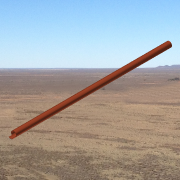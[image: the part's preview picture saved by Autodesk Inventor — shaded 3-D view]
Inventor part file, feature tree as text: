
AUTODESK INVENTOR PART (.ipt)
format: ipt  version: 2013 SP2 (Build 170200200, 200)  size: 152,576 bytes
history: native  units: in
note: dims shown in document units (in); Inventor stores cm internally (conversion verified against a paired STEP export)
features: sketch x4, extrude x3, plane x1
ambient origin geometry x8: Origin, YZ Plane, XZ Plane, XY Plane, X Axis, Y Axis, Z Axis, Center Point
feature tree (8):
  extrude  "Extrusion1"  Depth=0.785in
  extrude  "Extrusion2"  Depth=0.74in
  sketch  "Sketch3"  dims[d7=0.5in d8=0.0in d9=0.116in]
  plane  "Work Plane1"
  extrude  "Extrusion3"  Depth=0.116in
  sketch  "Sketch1"  dims[d0=0.875in d2=0.785in]
  sketch  "Sketch2"  dims[d3=25.59in d4=0.0in d5=0.74in]
  sketch  "Sketch4"  dims[d11=0.08in d12=0.5in d13=0.0in]
